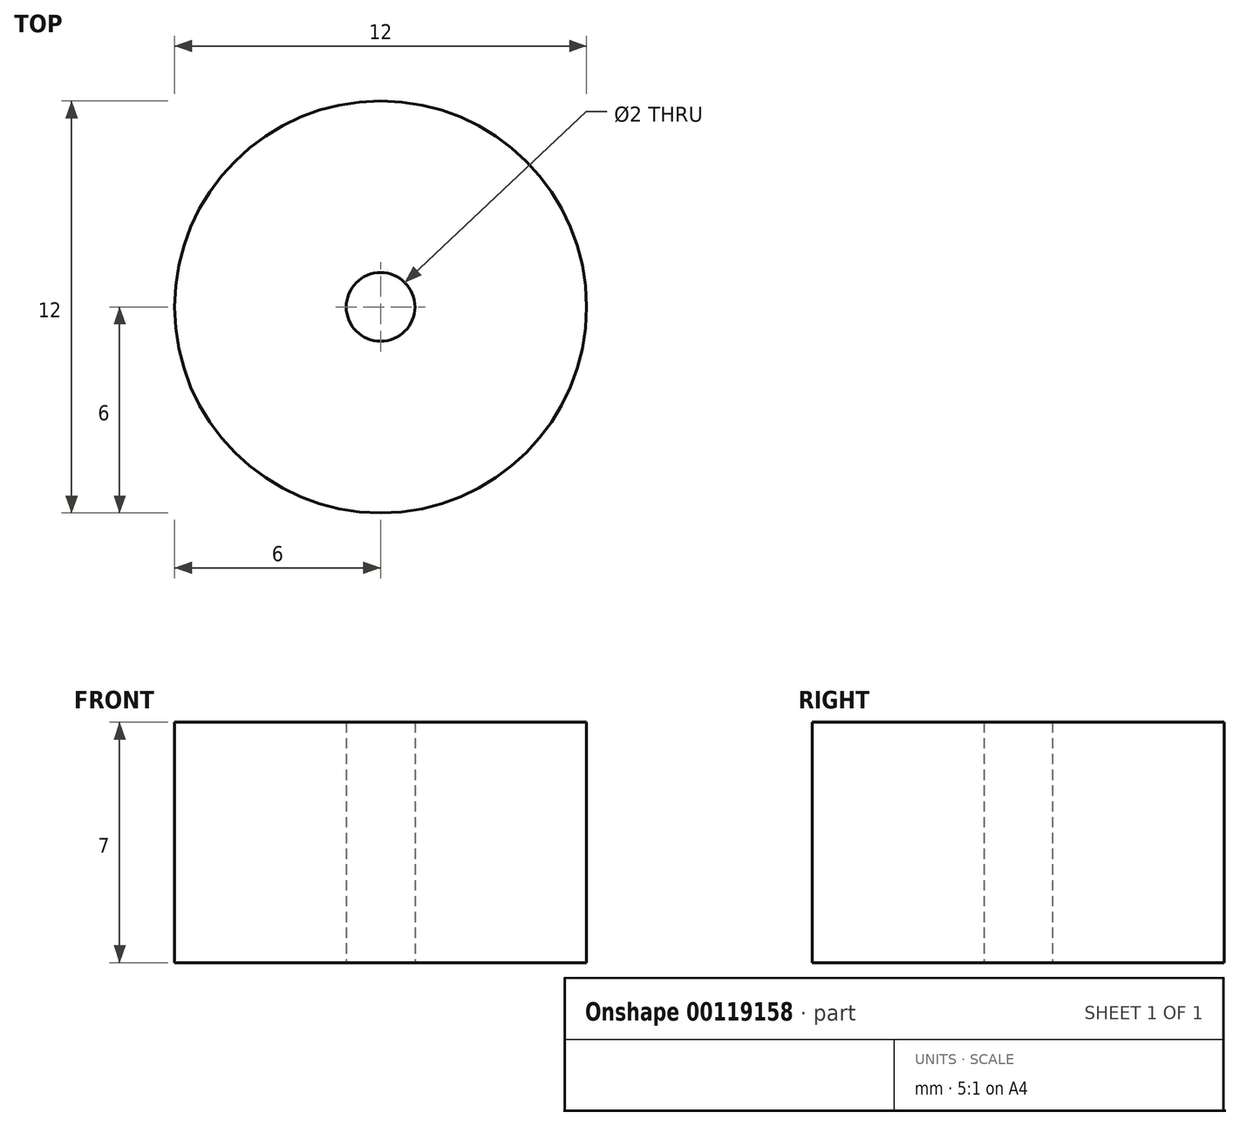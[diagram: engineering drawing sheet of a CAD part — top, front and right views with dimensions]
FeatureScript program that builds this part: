
annotation { "Feature Type Name" : "Feature", "Feature Type Description" : "" }
export const myFeature = defineFeature(function(context is Context, id is Id, definition is map)
    precondition{}
    {
        {
            var Q0;
            Q0=qCreatedBy(makeId("Top.planeOp"),FACE);
            var sketch = newSketch(context, id + "F0", { "sketchPlane" : qUnion([Q0])});
            skCircle(sketch, "E0", {"center": v(0, 0) * mm, "radius": 6 * mm});
            skPoint(sketch, "E1.orphan", {"position": v(-6, 0) * mm});
            skCircle(sketch, "E2", {"center": v(0, 0) * mm, "radius": 1 * mm});
            skSolve(sketch);
        }
        {
            var Q0;
            Q0=makeQuery(id+"F0.imprint","IMPRINT",FACE,{"disambiguationData":[TD([[makeQuery(id+"F0.imprint","IMPRINT",EDGE,{"derivedFrom":sQuery(id+"F0.wireOp",EDGE,"E0")}),1.0]])]});
            extrude(context, id + "F1", {"entities" : qUnion([Q0]), "endBound" : BoundingType.SYMMETRIC, "depth" : 7 * mm});
        }
    });
